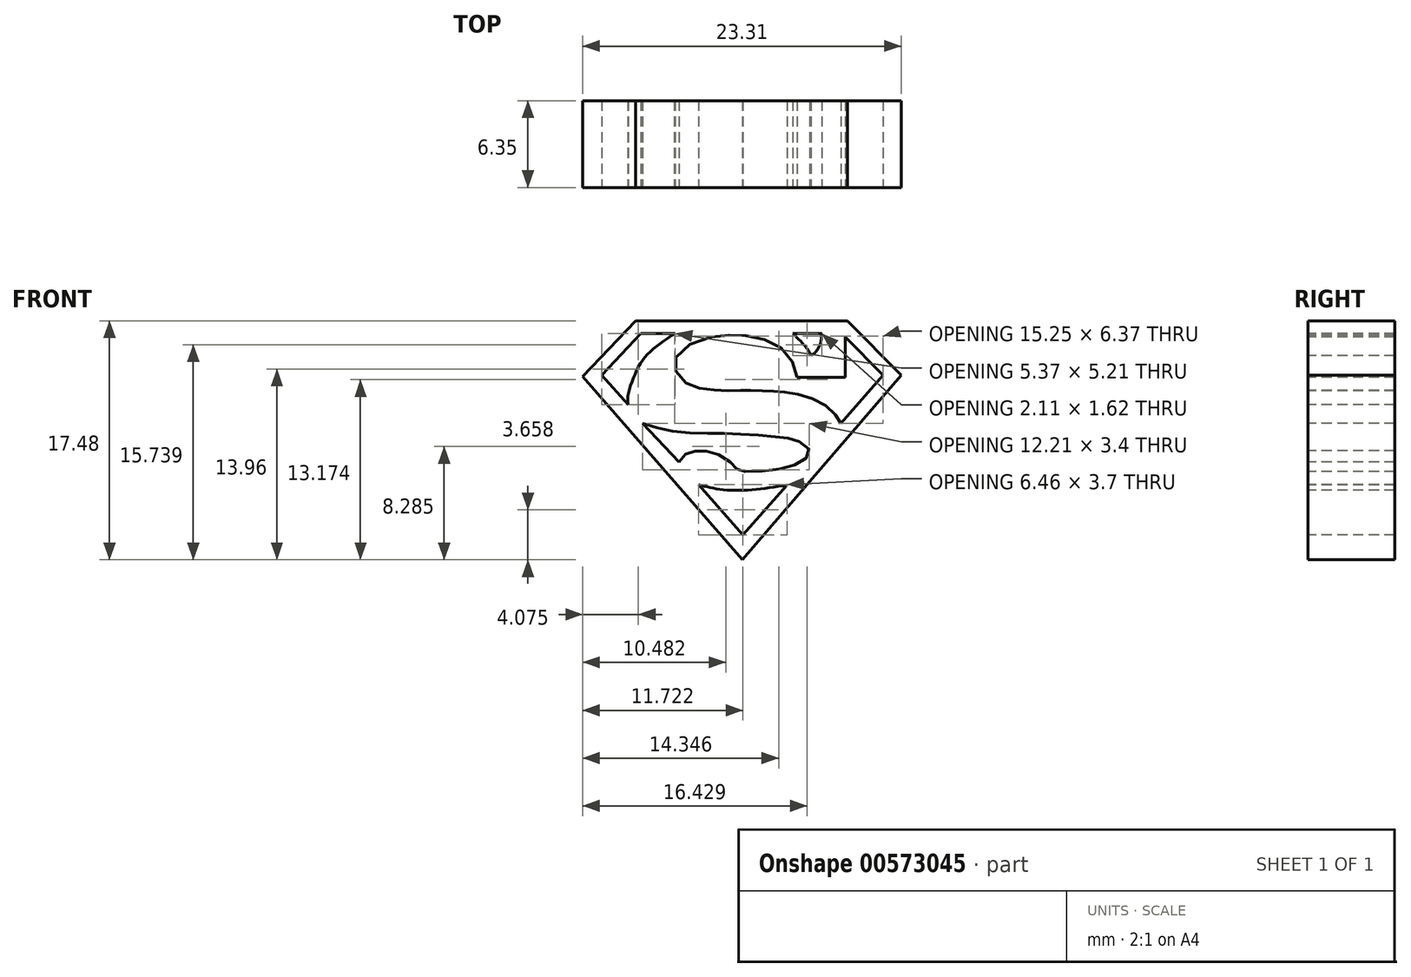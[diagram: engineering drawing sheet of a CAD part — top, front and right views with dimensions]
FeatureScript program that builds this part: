
annotation { "Feature Type Name" : "Feature", "Feature Type Description" : "" }
export const myFeature = defineFeature(function(context is Context, id is Id, definition is map)
    precondition{}
    {
        {
            var Q0;
            Q0=qCreatedBy(makeId("Front.planeOp"),FACE);
            var sketch = newSketch(context, id + "F0", { "sketchPlane" : qUnion([Q0])});
            skLineSegment(sketch, "E0", {"start": v(0, 0) * mm, "end": v(0, 25.4) * mm});
            skLineSegment(sketch, "E1", {"start": v(0, 25.4) * mm, "end": v(25.4, 25.4) * mm});
            skLineSegment(sketch, "E2", {"start": v(25.4, 25.4) * mm, "end": v(25.4, 0) * mm});
            skLineSegment(sketch, "E3", {"start": v(25.4, 0) * mm, "end": v(0, 0) * mm});
            skSolve(sketch);
        }
        {
            var Q0;
            Q0 = qSketchRegion(id + "F0", true);
            extrude(context, id + "F1", {"entities" : qUnion([Q0]), "depth" : 6.35 * mm, "offsetDistance" : 25.4 * mm});
        }
        {
            var Q0;
            Q0=makeQuery(id+"F1.opExtrude","CAP_FACE",FACE,{"disambiguationData":[OSD([sQuery(id+"F0.wireOp",EDGE,"E0"),sQuery(id+"F0.wireOp",EDGE,"E1"),sQuery(id+"F0.wireOp",EDGE,"E2"),sQuery(id+"F0.wireOp",EDGE,"E3")])],"isStart":false});
            var sketch = newSketch(context, id + "F2", { "sketchPlane" : qUnion([Q0])});
            skLineSegment(sketch, "E4", {"start": v(4.73, 18.97) * mm, "end": v(20.63, 18.97) * mm});
            skLineSegment(sketch, "E5", {"start": v(20.63, 18.97) * mm, "end": v(24.95, 14.54) * mm});
            skLineSegment(sketch, "E6", {"start": v(24.95, 14.54) * mm, "end": v(12.72, 0.33) * mm});
            skLineSegment(sketch, "E7", {"start": v(12.72, 0.33) * mm, "end": v(0.33, 14.54) * mm});
            skFitSpline(sketch, "E8", {"points": [v(8.08, 8.2) * mm, v(8.73, 8.85) * mm, v(9.74, 9) * mm, v(11.07, 8.68) * mm, v(12.24, 7.8) * mm, v(12.48, 7.56) * mm, v(14.74, 7.6) * mm, v(16.88, 8.12) * mm, v(17.64, 9) * mm, v(16.68, 9.77) * mm, v(15.47, 10.02) * mm, v(12.84, 10.22) * mm, v(10.38, 10.3) * mm, v(7.52, 10.46) * mm, v(5.42, 11.03) * mm], "startDerivative": vector(10.55, 13.9) * mm, "endDerivative": vector(-23.62, 7.93) * mm});
            skLineSegment(sketch, "E9", {"start": v(5.42, 11.03) * mm, "end": v(8.08, 8.2) * mm});
            skLineSegment(sketch, "E10", {"start": v(4.37, 12.4) * mm, "end": v(2.43, 14.54) * mm});
            skLineSegment(sketch, "E11", {"start": v(2.43, 14.54) * mm, "end": v(5.3, 17.6) * mm});
            skLineSegment(sketch, "E12", {"start": v(5.3, 17.6) * mm, "end": v(7.8, 17.6) * mm});
            skFitSpline(sketch, "E13", {"points": [v(4.37, 12.4) * mm, v(4.37, 13.12) * mm, v(4.77, 14.37) * mm, v(5.38, 15.58) * mm, v(6.39, 16.6) * mm, v(7.8, 17.6) * mm], "startDerivative": vector(-0.43, 4.52) * mm, "endDerivative": vector(6.31, 4.29) * mm});
            skLineSegment(sketch, "E14", {"start": v(9.53, 6.55) * mm, "end": v(12.76, 2.85) * mm});
            skLineSegment(sketch, "E15", {"start": v(12.76, 2.85) * mm, "end": v(15.99, 6.5) * mm});
            skFitSpline(sketch, "E16", {"points": [v(9.53, 6.55) * mm, v(10.87, 6.22) * mm, v(13.12, 6.14) * mm, v(15.99, 6.5) * mm], "startDerivative": vector(4.65, -1.37) * mm, "endDerivative": vector(7.47, 1.19) * mm});
            skLineSegment(sketch, "E17", {"start": v(16.41, 17.59) * mm, "end": v(18.52, 17.59) * mm});
            skFitSpline(sketch, "E18", {"points": [v(16.41, 17.59) * mm, v(16.56, 17.46) * mm, v(16.75, 17.27) * mm, v(17.05, 16.97) * mm, v(17.36, 16.6) * mm, v(17.62, 16.24) * mm, v(17.74, 15.97) * mm], "startDerivative": vector(1.14, -0.95) * mm, "endDerivative": vector(0.64, -1.7) * mm});
            skFitSpline(sketch, "E19", {"points": [v(17.74, 15.97) * mm, v(17.84, 16.03) * mm, v(17.98, 16.13) * mm, v(18.13, 16.3) * mm, v(18.3, 16.56) * mm, v(18.44, 16.88) * mm, v(18.5, 17.32) * mm, v(18.52, 17.59) * mm], "startDerivative": vector(1, 0.53) * mm, "endDerivative": vector(0.07, 1.68) * mm});
            skLineSegment(sketch, "E20", {"start": v(16.72, 14.39) * mm, "end": v(20.25, 14.39) * mm});
            skLineSegment(sketch, "E21", {"start": v(20.25, 14.39) * mm, "end": v(20.25, 17.35) * mm});
            skLineSegment(sketch, "E22", {"start": v(20.25, 17.35) * mm, "end": v(23.01, 14.54) * mm});
            skLineSegment(sketch, "E23", {"start": v(23.01, 14.54) * mm, "end": v(19.92, 11.03) * mm});
            skFitSpline(sketch, "E24", {"points": [v(19.92, 11.03) * mm, v(19.82, 11.26) * mm, v(19.62, 11.54) * mm, v(19.36, 11.85) * mm, v(18.98, 12.22) * mm, v(18.2, 12.68) * mm, v(17.79, 12.86) * mm, v(17.13, 13.07) * mm, v(16.54, 13.2) * mm, v(16.01, 13.3) * mm, v(15.45, 13.35) * mm, v(15.2, 13.38) * mm, v(14.8, 13.39) * mm, v(14.44, 13.4) * mm, v(14.04, 13.42) * mm, v(13.6, 13.43) * mm, v(13.28, 13.42) * mm, v(13, 13.42) * mm, v(12.68, 13.42) * mm, v(12.36, 13.42) * mm, v(11.75, 13.41) * mm, v(11.14, 13.42) * mm, v(10.6, 13.46) * mm, v(9.96, 13.53) * mm, v(9.31, 13.68) * mm, v(8.7, 13.92) * mm, v(8.15, 14.34) * mm, v(7.82, 14.95) * mm, v(7.76, 15.53) * mm, v(8.14, 16.27) * mm, v(9.33, 17) * mm, v(10.7, 17.38) * mm, v(11.67, 17.47) * mm, v(12.51, 17.46) * mm, v(13.4, 17.37) * mm, v(14.48, 17.11) * mm, v(15.44, 16.61) * mm, v(16.1, 15.98) * mm, v(16.58, 15.09) * mm, v(16.72, 14.39) * mm], "startDerivative": vector(-5.38, 14) * mm, "endDerivative": vector(3.46, -24.46) * mm});
            skLineSegment(sketch, "E25", {"start": v(0.33, 14.54) * mm, "end": v(4.73, 18.97) * mm});
            skLineSegment(sketch, "E26", {"start": v(4.92, 18.52) * mm, "end": v(20.42, 18.52) * mm});
            skLineSegment(sketch, "E27", {"start": v(20.42, 18.52) * mm, "end": v(24.35, 14.53) * mm});
            skLineSegment(sketch, "E28", {"start": v(24.35, 14.53) * mm, "end": v(12.74, 1.04) * mm});
            skLineSegment(sketch, "E29", {"start": v(12.74, 1.04) * mm, "end": v(1.04, 14.46) * mm});
            skLineSegment(sketch, "E30", {"start": v(1.04, 14.46) * mm, "end": v(4.92, 18.52) * mm});
            skSolve(sketch);
        }
        {
            var Q0;
            Q0=makeQuery(id+"F2.imprint","IMPRINT",FACE,{"disambiguationData":[TD([[makeQuery(id+"F2.imprint","IMPRINT",EDGE,{"derivedFrom":sQuery(id+"F2.wireOp",EDGE,"E10")}),-1.0]])]});
            var Q1;
            Q1=makeQuery(id+"F2.imprint","IMPRINT",FACE,{"disambiguationData":[TD([[makeQuery(id+"F2.imprint","IMPRINT",EDGE,{"derivedFrom":sQuery(id+"F2.wireOp",EDGE,"E20")}),-1.0]])]});
            var Q2;
            Q2=makeQuery(id+"F2.imprint","IMPRINT",FACE,{"disambiguationData":[TD([[makeQuery(id+"F2.imprint","IMPRINT",EDGE,{"derivedFrom":sQuery(id+"F2.wireOp",EDGE,"E17")}),-1.0]])]});
            var Q3;
            Q3=makeQuery(id+"F2.imprint","IMPRINT",FACE,{"disambiguationData":[TD([[makeQuery(id+"F2.imprint","IMPRINT",EDGE,{"derivedFrom":sQuery(id+"F2.wireOp",EDGE,"E8")}),1.0]])]});
            var Q4;
            Q4=makeQuery(id+"F2.imprint","IMPRINT",FACE,{"disambiguationData":[TD([[makeQuery(id+"F2.imprint","IMPRINT",EDGE,{"derivedFrom":sQuery(id+"F2.wireOp",EDGE,"E14")}),1.0]])]});
            var Q5;
            Q5=makeQuery(id+"F2.imprint","IMPRINT",FACE,{"disambiguationData":[TD([[makeQuery(id+"F2.imprint","IMPRINT",EDGE,{"derivedFrom":sQuery(id+"F2.wireOp",EDGE,"E4")}),-1.0]])]});
            var Q6;
            Q6=makeQuery(id+"F2.imprint","IMPRINT",FACE,{"disambiguationData":[TD([[makeQuery(id+"F2.imprint","IMPRINT",EDGE,{"derivedFrom":sQuery(id+"F2.wireOp",EDGE,"E4")}),1.0]])]});
            extrude(context, id + "F3", {"entities" : qUnion([Q0, Q1, Q2, Q3, Q4, Q5, Q6]), "operationType" : NewBodyOperationType.REMOVE, "oppositeDirection" : true, "depth" : 25.4 * mm, "offsetDistance" : 25.4 * mm});
        }
    });
